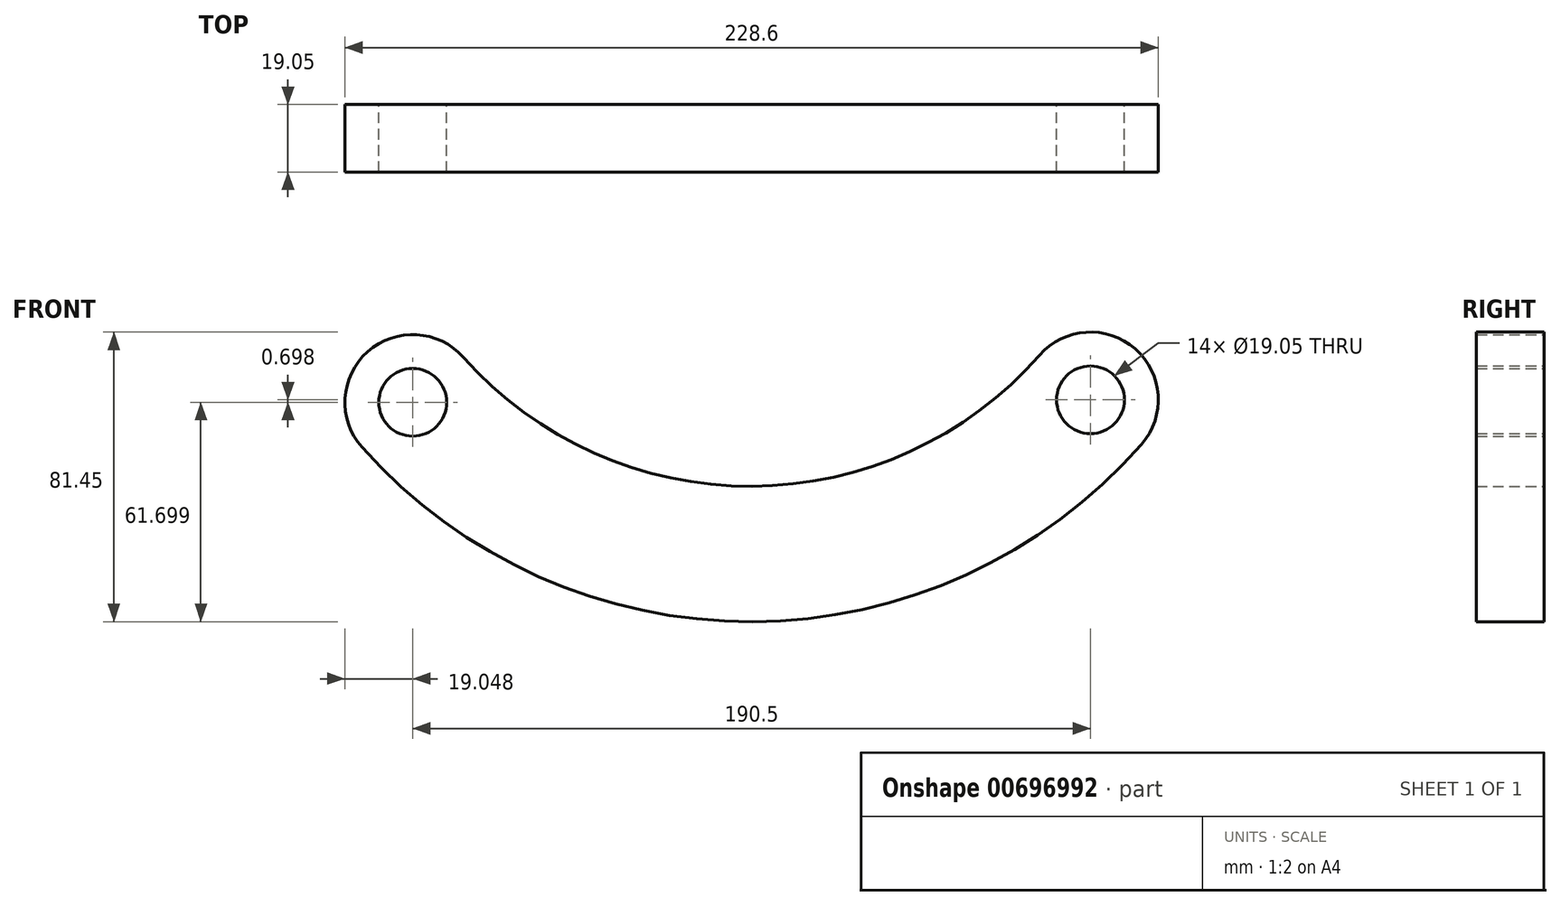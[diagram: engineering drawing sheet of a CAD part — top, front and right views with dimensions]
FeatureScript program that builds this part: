
annotation { "Feature Type Name" : "Feature", "Feature Type Description" : "" }
export const myFeature = defineFeature(function(context is Context, id is Id, definition is map)
    precondition{}
    {
        {
            var Q0;
            Q0=qCreatedBy(makeId("Front.planeOp"),FACE);
            var sketch = newSketch(context, id + "F0", { "sketchPlane" : qUnion([Q0])});
            skArc(sketch, "E0", {"start": v(-106.5, -69.2) * mm, "mid": v(0.47, -127) * mm, "end": v(107, -68.42) * mm});
            skCircle(sketch, "E1", {"center": v(-94.94, -84.35) * mm, "radius": 9.53 * mm});
            skCircle(sketch, "E2", {"center": v(95.56, -83.65) * mm, "radius": 9.53 * mm});
            skCircle(sketch, "E3", {"center": v(-94.94, -84.35) * mm, "radius": 19.05 * mm});
            skCircle(sketch, "E4", {"center": v(95.56, -83.65) * mm, "radius": 19.05 * mm});
            skArc(sketch, "E5", {"start": v(-80.7, -71.7) * mm, "mid": v(0.4, -107.95) * mm, "end": v(81.22, -71.1) * mm});
            skArc(sketch, "E6", {"start": v(-109.18, -97) * mm, "mid": v(0.54, -146.05) * mm, "end": v(109.9, -96.2) * mm});
            skSolve(sketch);
        }
        {
            var Q0;
            Q0=qSketchRegion(id+"F0",true);
            extrude(context, id + "F1", {"entities" : qUnion([Q0]), "depth" : 19.05 * mm});
        }
    });
